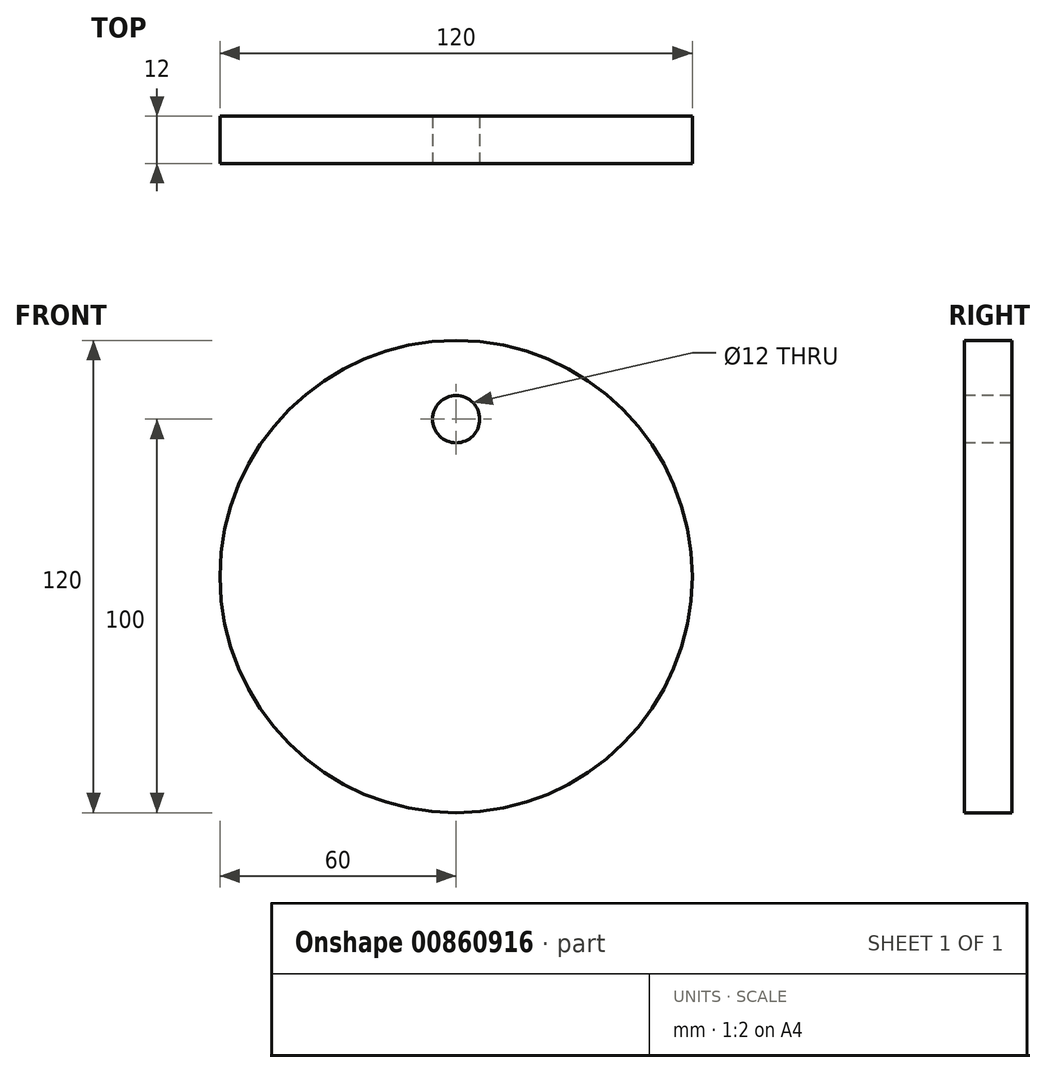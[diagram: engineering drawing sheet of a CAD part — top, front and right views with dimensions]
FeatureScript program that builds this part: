
annotation { "Feature Type Name" : "Feature", "Feature Type Description" : "" }
export const myFeature = defineFeature(function(context is Context, id is Id, definition is map)
    precondition{}
    {
        {
            assignVariable(context, id + "F0", {"name" : "baseplate", "anyValue" : 120});
        }
        {
            assignVariable(context, id + "F1", {"name" : "thickness", "anyValue" : getVariable(context, 'baseplate') / 10});
        }
        {
            var Q0;
            Q0=qCreatedBy(makeId("Front.planeOp"),FACE);
            var sketch = newSketch(context, id + "F2", { "sketchPlane" : qUnion([Q0])});
            skCircle(sketch, "E0", {"center": v(0, 0) * mm, "radius": 60 * mm});
            skSolve(sketch);
        }
        {
            var Q0;
            Q0 = qSketchRegion(id + "F2", true);
            extrude(context, id + "F3", {"entities" : qUnion([Q0]), "depth" : (getVariable(context, 'thickness')) * mm, "offsetDistance" : 25 * mm});
        }
        {
            var Q0;
            Q0=makeQuery(id+"F3.opExtrude","CAP_FACE",FACE,{"disambiguationData":[OSD([sQuery(id+"F2.wireOp",EDGE,"E0")])],"isStart":false});
            var sketch = newSketch(context, id + "F4", { "sketchPlane" : qUnion([Q0])});
            skCircle(sketch, "E1", {"center": v(0, 0) * mm, "radius": 40 * mm, "construction": true});
            skCircle(sketch, "E2", {"center": v(0, 40) * mm, "radius": 6 * mm});
            skSolve(sketch);
        }
        {
            var Q0;
            Q0 = qSketchRegion(id + "F4", true);
            extrude(context, id + "F5", {"entities" : qUnion([Q0]), "operationType" : NewBodyOperationType.REMOVE, "endBound" : BoundingType.THROUGH_ALL, "oppositeDirection" : true, "depth" : 25 * mm, "offsetDistance" : 25 * mm});
        }
    });
